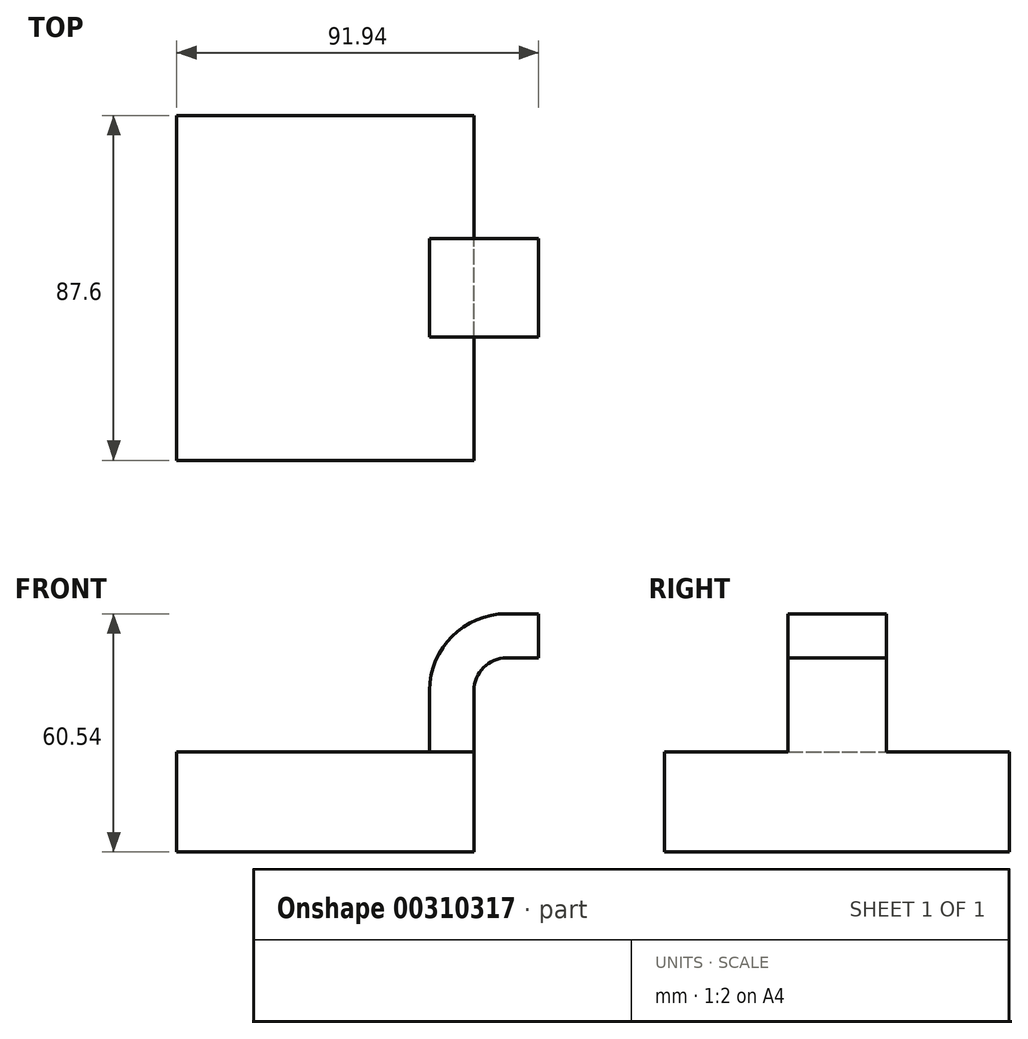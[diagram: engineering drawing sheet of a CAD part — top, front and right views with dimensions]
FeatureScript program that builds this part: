
annotation { "Feature Type Name" : "Feature", "Feature Type Description" : "" }
export const myFeature = defineFeature(function(context is Context, id is Id, definition is map)
    precondition{}
    {
        {
            var Q0;
            Q0=qCreatedBy(makeId("Front.planeOp"),FACE);
            var sketch = newSketch(context, id + "F0", { "sketchPlane" : qUnion([Q0])});
            skLineSegment(sketch, "E0.bottom", {"start": v(-37.75, 12.72) * mm, "end": v(37.75, 12.72) * mm});
            skLineSegment(sketch, "E0.top", {"start": v(-37.75, -12.72) * mm, "end": v(37.75, -12.72) * mm});
            skLineSegment(sketch, "E0.left", {"start": v(-37.75, 12.72) * mm, "end": v(-37.75, -12.72) * mm});
            skLineSegment(sketch, "E0.right", {"start": v(37.75, 12.72) * mm, "end": v(37.75, -12.72) * mm});
            skPoint(sketch, "E0.middle", {"position": v(0, 0) * mm});
            skLineSegment(sketch, "E1", {"start": v(37.75, 12.72) * mm, "end": v(37.75, 28.31) * mm});
            skArc(sketch, "E2", {"start": v(37.75, 28.31) * mm, "mid": v(40.17, 34.16) * mm, "end": v(46, 36.58) * mm});
            skLineSegment(sketch, "E3.bottom", {"start": v(54.19, 52.36) * mm, "end": v(91.4, 52.36) * mm});
            skLineSegment(sketch, "E3.top", {"start": v(54.19, 33.58) * mm, "end": v(91.4, 33.58) * mm});
            skLineSegment(sketch, "E3.left", {"start": v(54.19, 52.36) * mm, "end": v(54.19, 33.58) * mm});
            skLineSegment(sketch, "E3.right", {"start": v(91.4, 52.36) * mm, "end": v(91.4, 33.58) * mm});
            skPoint(sketch, "E3.middle", {"position": v(72.8, 42.97) * mm});
            skLineSegment(sketch, "E4", {"start": v(46, 36.58) * mm, "end": v(72.8, 36.58) * mm});
            skPoint(sketch, "E4.endSnap0", {"position": v(72.8, 33.58) * mm});
            skLineSegment(sketch, "E5.0", {"start": v(46, 47.82) * mm, "end": v(72.8, 47.82) * mm});
            skArc(sketch, "E5.1", {"start": v(26.5, 28.31) * mm, "mid": v(32.22, 42.1) * mm, "end": v(46, 47.82) * mm});
            skLineSegment(sketch, "E5.2", {"start": v(26.5, 12.72) * mm, "end": v(26.5, 28.31) * mm});
            skLineSegment(sketch, "E6", {"start": v(72.8, 33.58) * mm, "end": v(72.8, 52.36) * mm});
            skFitSpline(sketch, "E7", {"points": [v(-37.75, 12.72) * mm, v(46, 47.82) * mm], "startDerivative": vector(65.14, 89.07) * mm, "endDerivative": vector(89.07, -2.12) * mm});
            skSolve(sketch);
        }
        {
            var Q0;
            {var subQ5=sQuery(id+"F0.wireOp",EDGE,"E1");Q0=makeQuery(id+"F0.imprint","IMPRINT",FACE,{"disambiguationData":[TD([[makeQuery(id+"F0.imprint","IMPRINT",EDGE,{"derivedFrom":subQ5}),1.0]])]});}
            extrude(context, id + "F1", {"entities" : qUnion([Q0]), "endBound" : BoundingType.SYMMETRIC, "depth" : 25 * mm});
        }
        {
            var Q0;
            Q0=makeQuery(id+"F0.imprint","IMPRINT",FACE,{"disambiguationData":[TD([[makeQuery(id+"F0.imprint","IMPRINT",EDGE,{"derivedFrom":sQuery(id+"F0.wireOp",EDGE,"E0.top")}),1.0]])]});
            extrude(context, id + "F2", {"entities" : qUnion([Q0]), "operationType" : NewBodyOperationType.ADD, "endBound" : BoundingType.SYMMETRIC, "depth" : 87.6 * mm});
        }
    });
